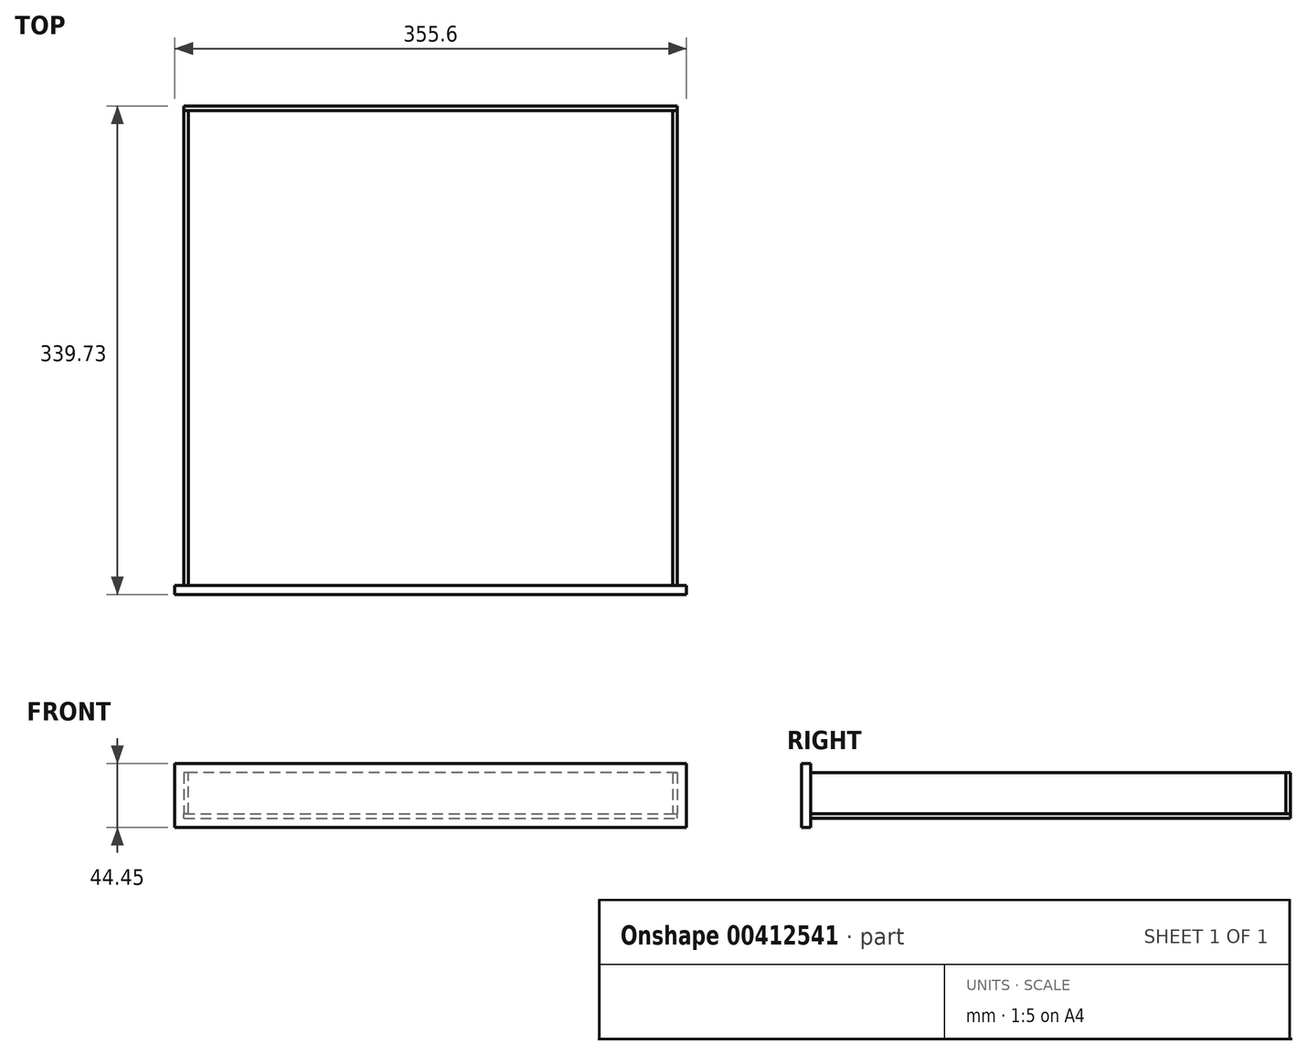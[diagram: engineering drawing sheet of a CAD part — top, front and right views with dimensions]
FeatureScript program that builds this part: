
annotation { "Feature Type Name" : "Feature", "Feature Type Description" : "" }
export const myFeature = defineFeature(function(context is Context, id is Id, definition is map)
    precondition{}
    {
        {
            var Q0;
            Q0=qCreatedBy(makeId("Front.planeOp"),FACE);
            var sketch = newSketch(context, id + "F0", { "sketchPlane" : qUnion([Q0])});
            skLineSegment(sketch, "E0.bottom", {"start": v(0, 0) * mm, "end": v(355.6, 0) * mm});
            skLineSegment(sketch, "E0.top", {"start": v(0, 44.45) * mm, "end": v(355.6, 44.45) * mm});
            skLineSegment(sketch, "E0.left", {"start": v(0, 0) * mm, "end": v(0, 44.45) * mm});
            skLineSegment(sketch, "E0.right", {"start": v(355.6, 0) * mm, "end": v(355.6, 44.45) * mm});
            skSolve(sketch);
        }
        {
            var Q0;
            Q0 = qSketchRegion(id + "F0", true);
            extrude(context, id + "F1", {"entities" : qUnion([Q0]), "depth" : 6.35 * mm});
        }
        {
            var Q0;
            Q0=makeQuery(id+"F1.opExtrude","SWEPT_FACE",FACE,{"disambiguationData":[OSD([sQuery(id+"F0.wireOp",EDGE,"E0.right")])]});
            cPlane(context, id + "F2", {"entities" : qUnion([Q0]), "cplaneType" : CPlaneType.OFFSET, "offset" : 6.35 * mm, "oppositeDirection" : true, "width" : 152.4 * mm, "height" : 152.4 * mm});
        }
        {
            var Q0;
            Q0=makeQuery(id+"F1.opExtrude","SWEPT_FACE",FACE,{"disambiguationData":[OSD([sQuery(id+"F0.wireOp",EDGE,"E0.left")])]});
            cPlane(context, id + "F3", {"entities" : qUnion([Q0]), "cplaneType" : CPlaneType.OFFSET, "offset" : 6.35 * mm, "oppositeDirection" : true, "width" : 152.4 * mm, "height" : 152.4 * mm});
        }
        {
            var Q0;
            Q0=qCreatedBy(id+"F2.planeOp",FACE);
            var sketch = newSketch(context, id + "F4", { "sketchPlane" : qUnion([Q0])});
            skLineSegment(sketch, "E1.bottom", {"start": v(0, 38.1) * mm, "end": v(330.2, 38.1) * mm});
            skLineSegment(sketch, "E1.top", {"start": v(0, 9.52) * mm, "end": v(330.2, 9.52) * mm});
            skLineSegment(sketch, "E1.left", {"start": v(0, 38.1) * mm, "end": v(0, 9.52) * mm});
            skLineSegment(sketch, "E1.right", {"start": v(330.2, 38.1) * mm, "end": v(330.2, 9.52) * mm});
            skSolve(sketch);
        }
        {
            var Q0;
            Q0 = qSketchRegion(id + "F4", true);
            extrude(context, id + "F5", {"entities" : qUnion([Q0]), "oppositeDirection" : true, "depth" : 3.17 * mm});
        }
        {
            var Q0;
            Q0=qCreatedBy(id+"F3.planeOp",FACE);
            var sketch = newSketch(context, id + "F6", { "sketchPlane" : qUnion([Q0])});
            skLineSegment(sketch, "E2.0.0", {"start": v(0, 9.52) * mm, "end": v(0, 38.1) * mm});
            skLineSegment(sketch, "E2.0.1", {"start": v(0, 38.1) * mm, "end": v(-330.2, 38.1) * mm});
            skLineSegment(sketch, "E2.0.2", {"start": v(-330.2, 38.1) * mm, "end": v(-330.2, 9.52) * mm});
            skLineSegment(sketch, "E2.0.3", {"start": v(-330.2, 9.52) * mm, "end": v(0, 9.52) * mm});
            skSolve(sketch);
        }
        {
            var Q0;
            Q0 = qSketchRegion(id + "F6", true);
            extrude(context, id + "F7", {"entities" : qUnion([Q0]), "oppositeDirection" : true, "depth" : 3.18 * mm});
        }
        {
            var Q0;
            Q0=makeQuery(id+"F5.opExtrude","SWEPT_FACE",FACE,{"disambiguationData":[OSD([sQuery(id+"F4.wireOp",EDGE,"E1.right")])]});
            var sketch = newSketch(context, id + "F8", { "sketchPlane" : qUnion([Q0])});
            skPoint(sketch, "E3.0", {"position": v(-349.25, 38.1) * mm});
            skPoint(sketch, "E4.0", {"position": v(-6.35, 9.52) * mm});
            skLineSegment(sketch, "E5.bottom", {"start": v(-349.25, 38.1) * mm, "end": v(-6.35, 38.1) * mm});
            skLineSegment(sketch, "E5.top", {"start": v(-349.25, 9.52) * mm, "end": v(-6.35, 9.52) * mm});
            skLineSegment(sketch, "E5.left", {"start": v(-349.25, 38.1) * mm, "end": v(-349.25, 9.52) * mm});
            skLineSegment(sketch, "E5.right", {"start": v(-6.35, 38.1) * mm, "end": v(-6.35, 9.52) * mm});
            skSolve(sketch);
        }
        {
            var Q0;
            Q0 = qSketchRegion(id + "F8", true);
            extrude(context, id + "F9", {"entities" : qUnion([Q0]), "depth" : 3.17 * mm});
        }
        {
            var Q0;
            Q0=makeQuery(id+"F9.opExtrude","SWEPT_FACE",FACE,{"disambiguationData":[OSD([sQuery(id+"F8.wireOp",EDGE,"E5.top")])]});
            var sketch = newSketch(context, id + "F10", { "sketchPlane" : qUnion([Q0])});
            skPoint(sketch, "E6.0", {"position": v(6.35, -333.38) * mm});
            skPoint(sketch, "E7.0", {"position": v(349.25, 0) * mm});
            skLineSegment(sketch, "E8.bottom", {"start": v(6.35, -333.38) * mm, "end": v(349.25, -333.38) * mm});
            skLineSegment(sketch, "E8.top", {"start": v(6.35, 0) * mm, "end": v(349.25, 0) * mm});
            skLineSegment(sketch, "E8.left", {"start": v(6.35, -333.38) * mm, "end": v(6.35, 0) * mm});
            skLineSegment(sketch, "E8.right", {"start": v(349.25, -333.38) * mm, "end": v(349.25, 0) * mm});
            skSolve(sketch);
        }
        {
            var Q0;
            Q0 = qSketchRegion(id + "F10", true);
            extrude(context, id + "F11", {"entities" : qUnion([Q0]), "depth" : 3.17 * mm});
        }
    });
